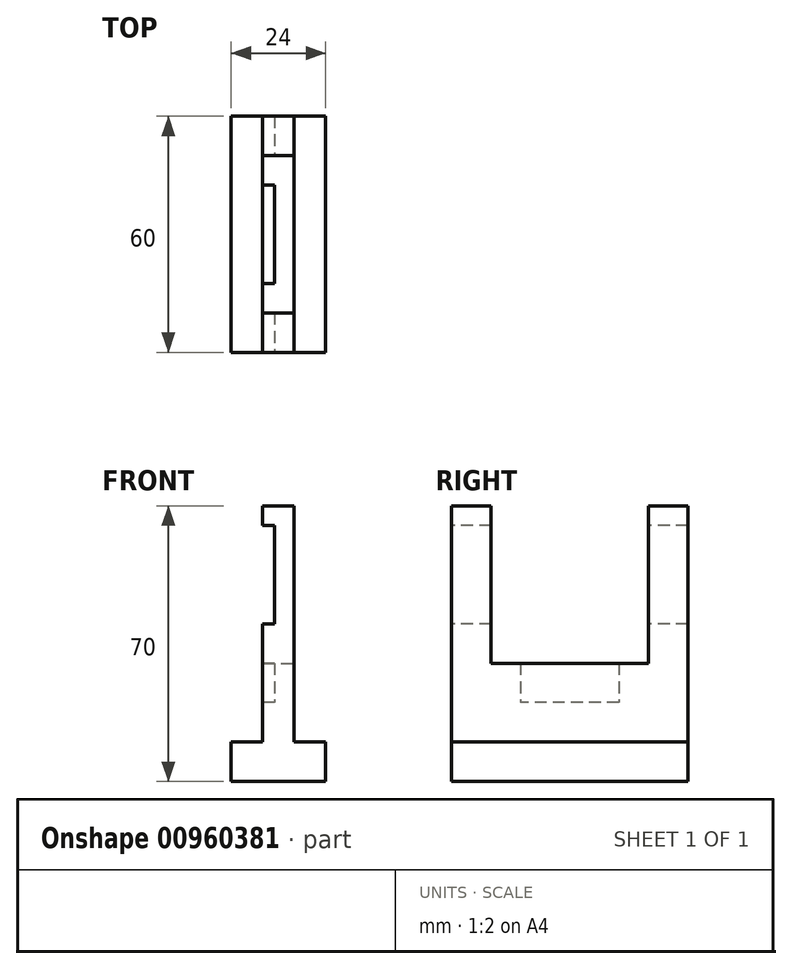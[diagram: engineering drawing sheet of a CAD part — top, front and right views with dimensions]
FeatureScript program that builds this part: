
annotation { "Feature Type Name" : "Feature", "Feature Type Description" : "" }
export const myFeature = defineFeature(function(context is Context, id is Id, definition is map)
    precondition{}
    {
        {
            var Q0;
            Q0=qCreatedBy(makeId("Right.planeOp"),FACE);
            var sketch = newSketch(context, id + "F0", { "sketchPlane" : qUnion([Q0])});
            skLineSegment(sketch, "E0.bottom", {"start": v(-30, 0) * mm, "end": v(30, 0) * mm});
            skLineSegment(sketch, "E0.left", {"start": v(-30, 0) * mm, "end": v(-30, 70) * mm});
            skLineSegment(sketch, "E0.right", {"start": v(30, 0) * mm, "end": v(30, 70) * mm});
            skLineSegment(sketch, "E1", {"start": v(-30, 70) * mm, "end": v(-20, 70) * mm});
            skLineSegment(sketch, "E2", {"start": v(-20, 70) * mm, "end": v(-20, 30) * mm});
            skLineSegment(sketch, "E3", {"start": v(-20, 30) * mm, "end": v(20, 30) * mm});
            skLineSegment(sketch, "E4", {"start": v(20, 30) * mm, "end": v(20, 70) * mm});
            skLineSegment(sketch, "E5", {"start": v(20, 70) * mm, "end": v(30, 70) * mm});
            skLineSegment(sketch, "E6.top", {"start": v(-30, 10) * mm, "end": v(30, 10) * mm});
            skLineSegment(sketch, "E6.left", {"start": v(-30, 0) * mm, "end": v(-30, 10) * mm});
            skLineSegment(sketch, "E6.right", {"start": v(30, 0) * mm, "end": v(30, 10) * mm});
            skSolve(sketch);
        }
        {
            var Q0;
            Q0 = qSketchRegion(id + "F0", true);
            extrude(context, id + "F1", {"entities" : qUnion([Q0]), "oppositeDirection" : true, "depth" : 8 * mm, "offsetDistance" : 25 * mm});
        }
        {
            var Q0;
            Q0=makeQuery(id+"F0.imprint","IMPRINT",FACE,{"disambiguationData":[TD([[makeQuery(id+"F0.imprint","IMPRINT",EDGE,{"derivedFrom":sQuery(id+"F0.wireOp",EDGE,"E0.bottom")}),1.0]])]});
            extrude(context, id + "F2", {"entities" : qUnion([Q0]), "operationType" : NewBodyOperationType.ADD, "depth" : 8 * mm, "offsetDistance" : 25 * mm});
        }
        {
            var Q0;
            Q0=makeQuery(id+"F1.opExtrude","CAP_FACE",FACE,{"disambiguationData":[OSD([sQuery(id+"F0.wireOp",EDGE,"E0.left"),sQuery(id+"F0.wireOp",EDGE,"E0.right"),sQuery(id+"F0.wireOp",EDGE,"E1"),sQuery(id+"F0.wireOp",EDGE,"E2"),sQuery(id+"F0.wireOp",EDGE,"E3"),sQuery(id+"F0.wireOp",EDGE,"E4"),sQuery(id+"F0.wireOp",EDGE,"E5"),sQuery(id+"F0.wireOp",EDGE,"E0.bottom"),sQuery(id+"F0.wireOp",EDGE,"E6.left"),sQuery(id+"F0.wireOp",EDGE,"E6.right")])],"isStart":false});
            var sketch = newSketch(context, id + "F3", { "sketchPlane" : qUnion([Q0])});
            skLineSegment(sketch, "E7.bottom", {"start": v(-30, 65) * mm, "end": v(-20, 65) * mm});
            skLineSegment(sketch, "E7.top", {"start": v(-30, 40) * mm, "end": v(-20, 40) * mm});
            skLineSegment(sketch, "E7.left", {"start": v(-30, 65) * mm, "end": v(-30, 40) * mm});
            skLineSegment(sketch, "E7.right", {"start": v(-20, 65) * mm, "end": v(-20, 40) * mm});
            skLineSegment(sketch, "E8.bottom", {"start": v(20, 65) * mm, "end": v(30, 65) * mm});
            skLineSegment(sketch, "E8.top", {"start": v(20, 40) * mm, "end": v(30, 40) * mm});
            skLineSegment(sketch, "E8.left", {"start": v(20, 65) * mm, "end": v(20, 40) * mm});
            skLineSegment(sketch, "E8.right", {"start": v(30, 65) * mm, "end": v(30, 40) * mm});
            skLineSegment(sketch, "E9.bottom", {"start": v(-12.5, 30) * mm, "end": v(12.5, 30) * mm});
            skLineSegment(sketch, "E9.top", {"start": v(-12.5, 20) * mm, "end": v(12.5, 20) * mm});
            skLineSegment(sketch, "E9.left", {"start": v(-12.5, 30) * mm, "end": v(-12.5, 20) * mm});
            skLineSegment(sketch, "E9.right", {"start": v(12.5, 30) * mm, "end": v(12.5, 20) * mm});
            skSolve(sketch);
        }
        {
            var Q0;
            Q0 = qSketchRegion(id + "F3", true);
            extrude(context, id + "F4", {"entities" : qUnion([Q0]), "operationType" : NewBodyOperationType.REMOVE, "oppositeDirection" : true, "depth" : 3 * mm, "offsetDistance" : 25 * mm});
        }
        {
            var Q0;
            Q0=makeQuery(id+"F0.imprint","IMPRINT",FACE,{"disambiguationData":[TD([[makeQuery(id+"F0.imprint","IMPRINT",EDGE,{"derivedFrom":sQuery(id+"F0.wireOp",EDGE,"E0.bottom")}),1.0]])]});
            extrude(context, id + "F5", {"entities" : qUnion([Q0]), "operationType" : NewBodyOperationType.ADD, "oppositeDirection" : true, "depth" : 16 * mm, "offsetDistance" : 25 * mm});
        }
    });
